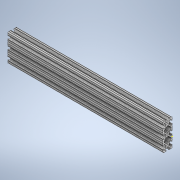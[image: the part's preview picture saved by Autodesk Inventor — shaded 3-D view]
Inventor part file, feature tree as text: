
AUTODESK INVENTOR PART (.ipt)
format: ipt  version: 2020 (Build 240168000, 168)  size: 376,832 bytes
history: native  units: in
note: dims shown in document units (in); Inventor stores cm internally (conversion verified against a paired STEP export)
features: sketch x2, extrude x1
ambient origin geometry x8: Origin, YZ Plane, XZ Plane, XY Plane, X Axis, Y Axis, Z Axis, Center Point
bodies: Solid1 (feature_tree)
feature tree (3):
  extrude  "Extrusion1"  [1 undecoded]
  sketch  "Sketch2"
  sketch  "Sketch1"  dims[d0=17.0in d1=0.0in]
note: 1 required parameter value undecoded (feature->parameter linkage not recoverable at this tier; creation-order binding heuristic only, values carry confidence <= 0.55)
